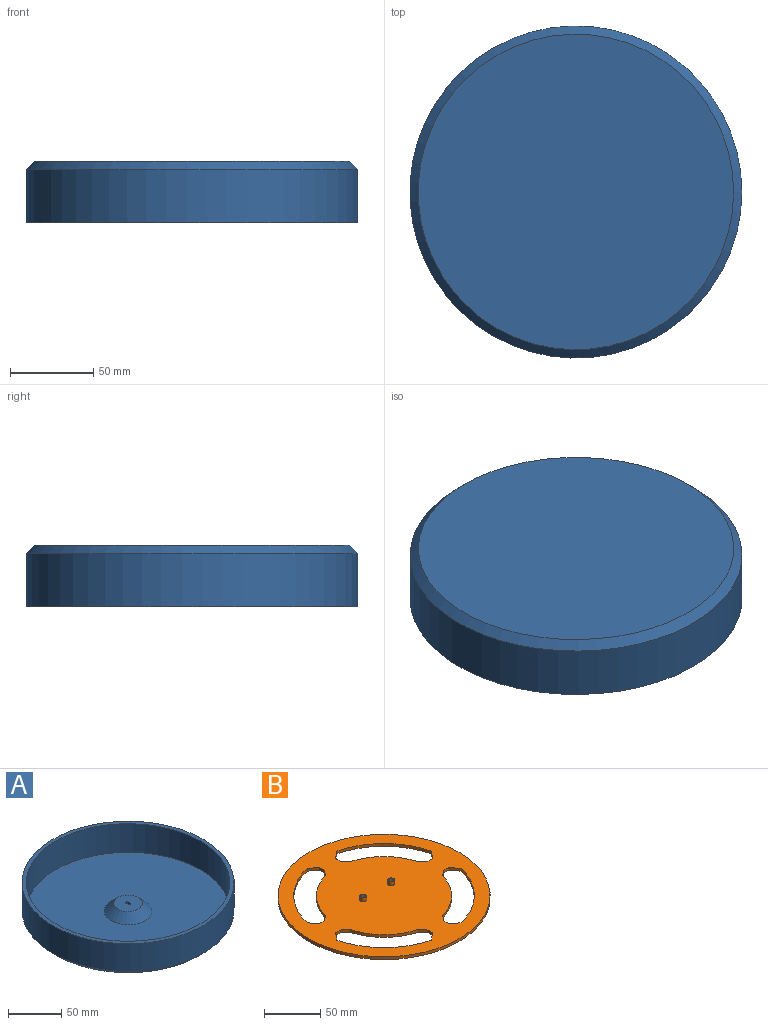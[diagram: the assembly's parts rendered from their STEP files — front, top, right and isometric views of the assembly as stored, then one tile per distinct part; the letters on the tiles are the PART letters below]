
ASSEMBLY  parts=2 mates=1
PART A: 13 faces, bbox 200x200x37 mm
  f0: cylinder r=96mm len=192mm, axis (0,0,-1), area 19905.1mm2, adj f1,f9
  f1: plane 192x192mm, normal (0,0,1), area 27362.5mm2, adj f0,f8
  f2: plane 4.9x2.9mm, normal (0,0,1), area 13.3mm2, adj f3,f4,f5,f6
  f3: plane 5.9x3.95mm, normal (-1,0,0), area 23.3mm2, adj f2,f4,f6,f7
  f4: cylinder r=2.45mm len=5.9mm, axis (0,0,1), area 18.3mm2, adj f2,f3,f5,f7
  f5: plane 5.9x3.95mm, normal (1,0,0), area 23.3mm2, adj f2,f4,f6,f7
  f6: cylinder r=2.45mm len=5.9mm, axis (0,0,1), area 18.3mm2, adj f2,f3,f5,f7
  f7: plane 27x27mm, normal (0,0,1), area 559.2mm2, adj f3,f4,f5,f6,f8
  f8: cone r=13.5mm half-angle=45deg, axis (0,0,-1), area 1439.5mm2, adj f1,f7
  f9: plane 200x200mm, normal (0,0,1), area 2463mm2, adj f0,f12
  f10: plane 190x190mm, normal (0,0,-1), area 28352.9mm2, adj f11
  f11: cone r=100mm half-angle=45deg, axis (0,0,1), area 4331.8mm2, adj f10,f12
  f12: cylinder r=100mm len=200mm, axis (0,0,-1), area 20106.2mm2, adj f9,f11
PART B: 41 faces, bbox 188x188x7 mm
  f0: plane 188x188mm, normal (0,0,1), area 20929.7mm2, adj f2,f5,f7,f9,f10,f11,f12,f13
  f1: plane 188x188mm, normal (0,0,-1), area 20962.4mm2, adj f2,f3,f4,f9,f10,f11,f12,f13
  f2: cylinder r=94mm len=188mm, axis (0,0,-1), area 1771.9mm2, adj f0,f1
  f3: cylinder r=1.95mm len=7mm, axis (0,0,1), area 85.8mm2, adj f1,f8
  f4: cylinder r=1.95mm len=7mm, axis (0,0,1), area 85.8mm2, adj f1,f6
  f5: cylinder r=3mm len=6mm, axis (0,0,-1), area 75.4mm2, adj f0,f6
  f6: plane 6x6mm, normal (0,0,1), area 16.3mm2, adj f4,f5
  f7: cylinder r=3mm len=6mm, axis (0,0,-1), area 75.4mm2, adj f0,f8
  f8: plane 6x6mm, normal (0,0,1), area 16.3mm2, adj f3,f7
  f9: cylinder r=60mm len=42.77mm, axis (0,0,1), area 190.2mm2, adj f0,f1,f37,f39
  f10: plane 6.07x3mm, normal (-1,0,0), area 18.2mm2, adj f0,f1,f39,f40
  f11: cylinder r=80mm len=59.08mm, axis (0,0,1), area 263.7mm2, adj f0,f1,f38,f40
  f12: plane 6.07x3mm, normal (0,1,0), area 18.2mm2, adj f0,f1,f37,f38
  f13: plane 6.07x3mm, normal (1,0,0), area 18.2mm2, adj f0,f1,f25,f26
  f14: cylinder r=60mm len=42.77mm, axis (0,0,1), area 190.2mm2, adj f0,f1,f25,f28
  f15: plane 6.07x3mm, normal (0,1,0), area 18.2mm2, adj f0,f1,f27,f28
  f16: cylinder r=80mm len=59.08mm, axis (0,0,1), area 263.7mm2, adj f0,f1,f26,f27
  f17: plane 6.07x3mm, normal (1,0,0), area 18.2mm2, adj f0,f1,f31,f32
  f18: cylinder r=80mm len=59.08mm, axis (0,0,1), area 263.7mm2, adj f0,f1,f29,f32
  f19: plane 6.07x3mm, normal (0,-1,0), area 18.2mm2, adj f0,f1,f29,f30
  f20: cylinder r=60mm len=42.77mm, axis (0,0,1), area 190.2mm2, adj f0,f1,f30,f31
  f21: cylinder r=80mm len=59.08mm, axis (0,0,1), area 263.7mm2, adj f0,f1,f34,f36
  f22: plane 6.07x3mm, normal (-1,0,0), area 18.2mm2, adj f0,f1,f33,f34
  f23: cylinder r=60mm len=42.77mm, axis (0,0,1), area 190.2mm2, adj f0,f1,f33,f35
  f24: plane 6.07x3mm, normal (0,-1,0), area 18.2mm2, adj f0,f1,f35,f36
  f25: plane 6.82x5.26mm, normal (0.79,0.61,0), area 25.8mm2, adj f0,f1,f13,f14
  f26: plane 8.71x6.86mm, normal (0.62,-0.79,0), area 33.2mm2, adj f0,f1,f13,f16
  f27: plane 8.71x6.86mm, normal (-0.79,0.62,0), area 33.2mm2, adj f0,f1,f15,f16
  f28: plane 6.82x5.26mm, normal (0.61,0.79,0), area 25.8mm2, adj f0,f1,f14,f15
  f29: plane 8.71x6.86mm, normal (-0.79,-0.62,0), area 33.2mm2, adj f0,f1,f18,f19
  f30: plane 6.82x5.26mm, normal (0.61,-0.79,0), area 25.8mm2, adj f0,f1,f19,f20
  f31: plane 6.82x5.26mm, normal (0.79,-0.61,0), area 25.8mm2, adj f0,f1,f17,f20
  f32: plane 8.71x6.86mm, normal (0.62,0.79,0), area 33.2mm2, adj f0,f1,f17,f18
  f33: plane 6.82x5.26mm, normal (-0.79,-0.61,0), area 25.8mm2, adj f0,f1,f22,f23
  f34: plane 8.71x6.86mm, normal (-0.62,0.79,0), area 33.2mm2, adj f0,f1,f21,f22
  f35: plane 6.82x5.26mm, normal (-0.61,-0.79,0), area 25.8mm2, adj f0,f1,f23,f24
  f36: plane 8.71x6.86mm, normal (0.79,-0.62,0), area 33.2mm2, adj f0,f1,f21,f24
  f37: plane 6.82x5.26mm, normal (-0.61,0.79,0), area 25.8mm2, adj f0,f1,f9,f12
  f38: plane 8.71x6.86mm, normal (0.79,0.62,0), area 33.2mm2, adj f0,f1,f11,f12
  f39: plane 6.82x5.26mm, normal (-0.79,0.61,0), area 25.8mm2, adj f0,f1,f9,f10
  f40: plane 8.71x6.86mm, normal (-0.62,-0.79,0), area 33.2mm2, adj f0,f1,f10,f11
PLACE A rot(axis=(-1,0,0),180deg) t=(-16.35,-78.81,140.89)mm
PLACE B t=(-16.35,-78.81,106.39)mm
MATE slider B.f2 <-> A.f0  axis (0,0,-1) through (-16.35,-78.81,106.39)mm
